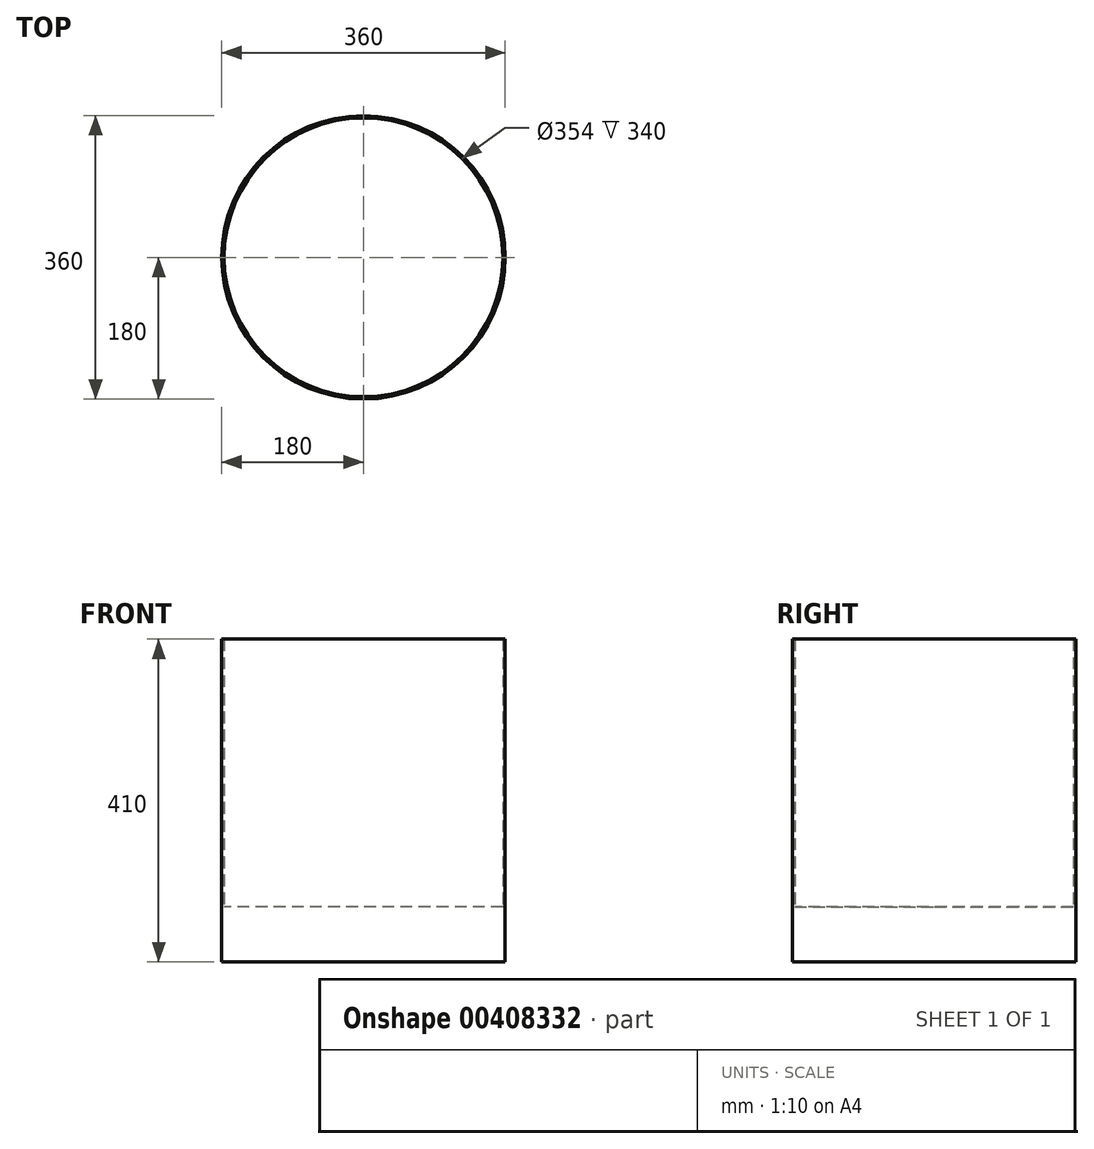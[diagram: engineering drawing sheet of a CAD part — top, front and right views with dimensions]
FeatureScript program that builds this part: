
annotation { "Feature Type Name" : "Feature", "Feature Type Description" : "" }
export const myFeature = defineFeature(function(context is Context, id is Id, definition is map)
    precondition{}
    {
        {
            var Q0;
            Q0=qCreatedBy(makeId("Top.planeOp"),FACE);
            var sketch = newSketch(context, id + "F0", { "sketchPlane" : qUnion([Q0])});
            skCircle(sketch, "E0", {"center": v(0, 0) * mm, "radius": 180 * mm});
            skSolve(sketch);
        }
        {
            var Q0;
            Q0=makeQuery(id+"F0.imprint","IMPRINT",FACE,{"disambiguationData":[TD([[makeQuery(id+"F0.imprint","IMPRINT",EDGE,{"derivedFrom":sQuery(id+"F0.wireOp",EDGE,"E0")}),1.0]])]});
            extrude(context, id + "F1", {"entities" : qUnion([Q0]), "depth" : 70 * mm});
        }
        {
            var Q0;
            Q0=makeQuery(id+"F1.opExtrude","CAP_FACE",FACE,{"disambiguationData":[OSD([sQuery(id+"F0.wireOp",EDGE,"E0")])],"isStart":false});
            var sketch = newSketch(context, id + "F2", { "sketchPlane" : qUnion([Q0])});
            skCircle(sketch, "E1", {"center": v(0, 0) * mm, "radius": 177 * mm});
            skSolve(sketch);
        }
        {
            var Q0;
            Q0=makeQuery(id+"F2.imprint","IMPRINT",FACE,{"disambiguationData":[TD([[makeQuery(id+"F2.imprint","IMPRINT",EDGE,{"derivedFrom":sQuery(id+"F2.wireOp",EDGE,"E1")}),-1.0]])]});
            extrude(context, id + "F3", {"entities" : qUnion([Q0]), "operationType" : NewBodyOperationType.ADD, "depth" : (410 - 70) * mm});
        }
    });
